FCSTD DOCUMENT  (FreeCAD 0.15R4671 (Git))
Label: basical measure
License: All rights reserved
LicenseURL: http://es.wikipedia.org/wiki/Todos_los_derechos_reservados
objects: Sketcher::SketchObject×1
note: 1 computed .brp shape members not serialized (recipe doc carries the construction recipe); baked Part::Feature solids carry a one-line shape summary decoded from their .brp

FEATURE [Sketcher::SketchObject] Sketch
  Placement = pos=(0,0,0) rot=(-1,0,0;4.71239rad)
  sketch-geometry (13):
    g0: LineSegment StartX=0 StartY=0 StartZ=0 EndX=38 EndY=0 EndZ=0
    g1: LineSegment StartX=38 StartY=0 StartZ=0 EndX=38 EndY=7.8 EndZ=0
    g2: LineSegment StartX=38 StartY=7.8 StartZ=0 EndX=52.9982 EndY=8.03263 EndZ=0
    g3: LineSegment StartX=0 StartY=0 StartZ=0 EndX=11.2382 EndY=-37.6589 EndZ=0
    g4: LineSegment StartX=52.9982 StartY=8.03263 StartZ=0 EndX=13.8405 EndY=39.124 EndZ=0
    g5: LineSegment StartX=13.8405 StartY=39.124 StartZ=0 EndX=0 EndY=0 EndZ=0
    g6: LineSegment StartX=0 StartY=0 StartZ=0 EndX=-36.8536 EndY=15.8057 EndZ=0
    g7: LineSegment StartX=-36.8536 StartY=15.8057 StartZ=0 EndX=13.8405 EndY=39.124 EndZ=0
    g8: LineSegment StartX=-36.8536 StartY=15.8057 StartZ=0 EndX=-21.1014 EndY=-20.3084 EndZ=0
    g9: LineSegment StartX=-21.1014 StartY=-20.3084 StartZ=0 EndX=11.2382 EndY=-37.6589 EndZ=0
    g10: LineSegment StartX=11.2382 StartY=-37.6589 StartZ=0 EndX=-4.80979 EndY=-83.9564 EndZ=0
    g11: LineSegment StartX=-4.80979 StartY=-83.9564 StartZ=0 EndX=-21.1014 EndY=-20.3084 EndZ=0
    g12: LineSegment StartX=11.2382 StartY=-37.6589 StartZ=0 EndX=52.9982 EndY=8.03263 EndZ=0
  constraints (33):
    c: Coincident(g-1,g0)
    c: Horizontal(g0)
    c: Coincident(g0,g1)
    c: Vertical(g1)
    c: Coincident(g1,g2)
    c: Coincident(g3,g-1)
    c: Coincident(g4,g2)
    c: Coincident(g5,g4)
    c: Coincident(g5,g-1)
    c: Coincident(g6,g-1)
    c: Coincident(g7,g6)
    c: Coincident(g7,g4)
    c: Coincident(g8,g6)
    c: Coincident(g8,g9)
    c: Coincident(g9,g3)
    c: Coincident(g9,g10)
    c: Coincident(g10,g11)
    c: Coincident(g11,g9)
    c: Coincident(g12,g3)
    c: Coincident(g12,g2)
    c: Distance(g7) = 55.8
    c: Distance(g6) = 40.1
    c: Distance(g5) = 41.5
    c: Distance(g4) = 50
    c: Distance(g8) = 39.4
    c: Distance(g3) = 39.3
    c: Distance(g9) = 36.7
    c: Distance(g11) = 65.7
    c: Distance(g10) = 49
    c: Distance(g12) = 61.9
    c: Distance(g0) = 38
    c: Distance(g1) = 7.8
    c: Distance(g2) = 15
